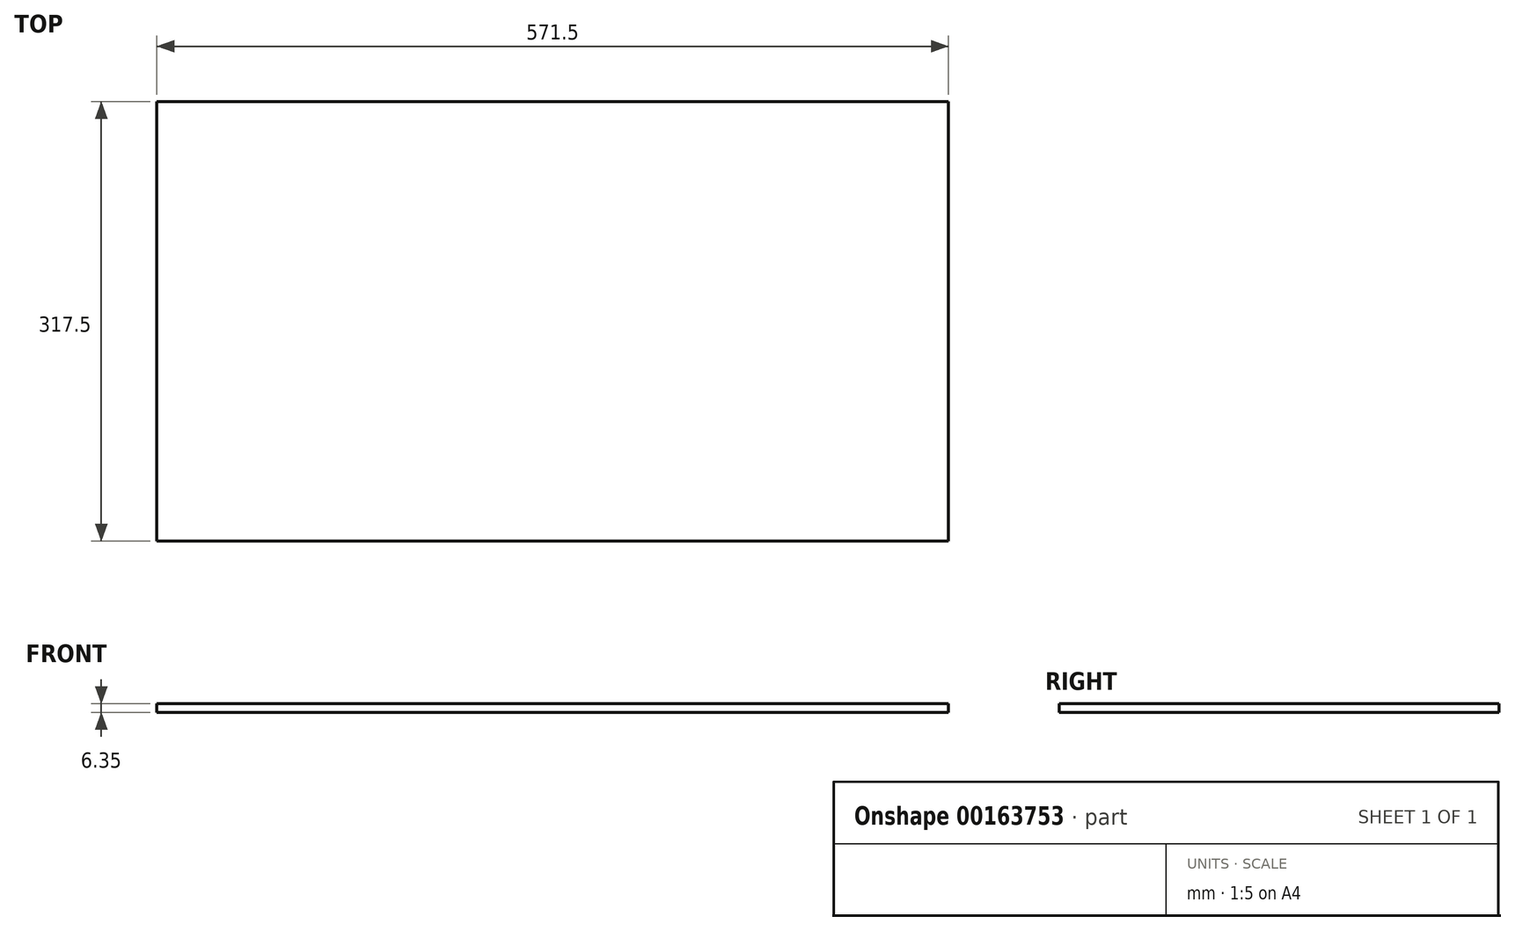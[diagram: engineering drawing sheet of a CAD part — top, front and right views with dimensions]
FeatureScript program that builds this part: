
annotation { "Feature Type Name" : "Feature", "Feature Type Description" : "" }
export const myFeature = defineFeature(function(context is Context, id is Id, definition is map)
    precondition{}
    {
        {
            var Q0;
            Q0=qCreatedBy(makeId("Top.planeOp"),FACE);
            var sketch = newSketch(context, id + "F0", { "sketchPlane" : qUnion([Q0])});
            skLineSegment(sketch, "E0.bottom", {"start": v(285.75, 158.75) * mm, "end": v(-285.75, 158.75) * mm});
            skLineSegment(sketch, "E0.top", {"start": v(285.75, -158.75) * mm, "end": v(-285.75, -158.75) * mm});
            skLineSegment(sketch, "E0.left", {"start": v(285.75, 158.75) * mm, "end": v(285.75, -158.75) * mm});
            skLineSegment(sketch, "E0.right", {"start": v(-285.75, 158.75) * mm, "end": v(-285.75, -158.75) * mm});
            skPoint(sketch, "E0.middle", {"position": v(0, 0) * mm});
            skSolve(sketch);
        }
        {
            var Q0;
            Q0=qSketchRegion(id+"F0",true);
            extrude(context, id + "F1", {"entities" : qUnion([Q0]), "depth" : 6.35 * mm, "offsetDistance" : 25.4 * mm});
        }
    });
